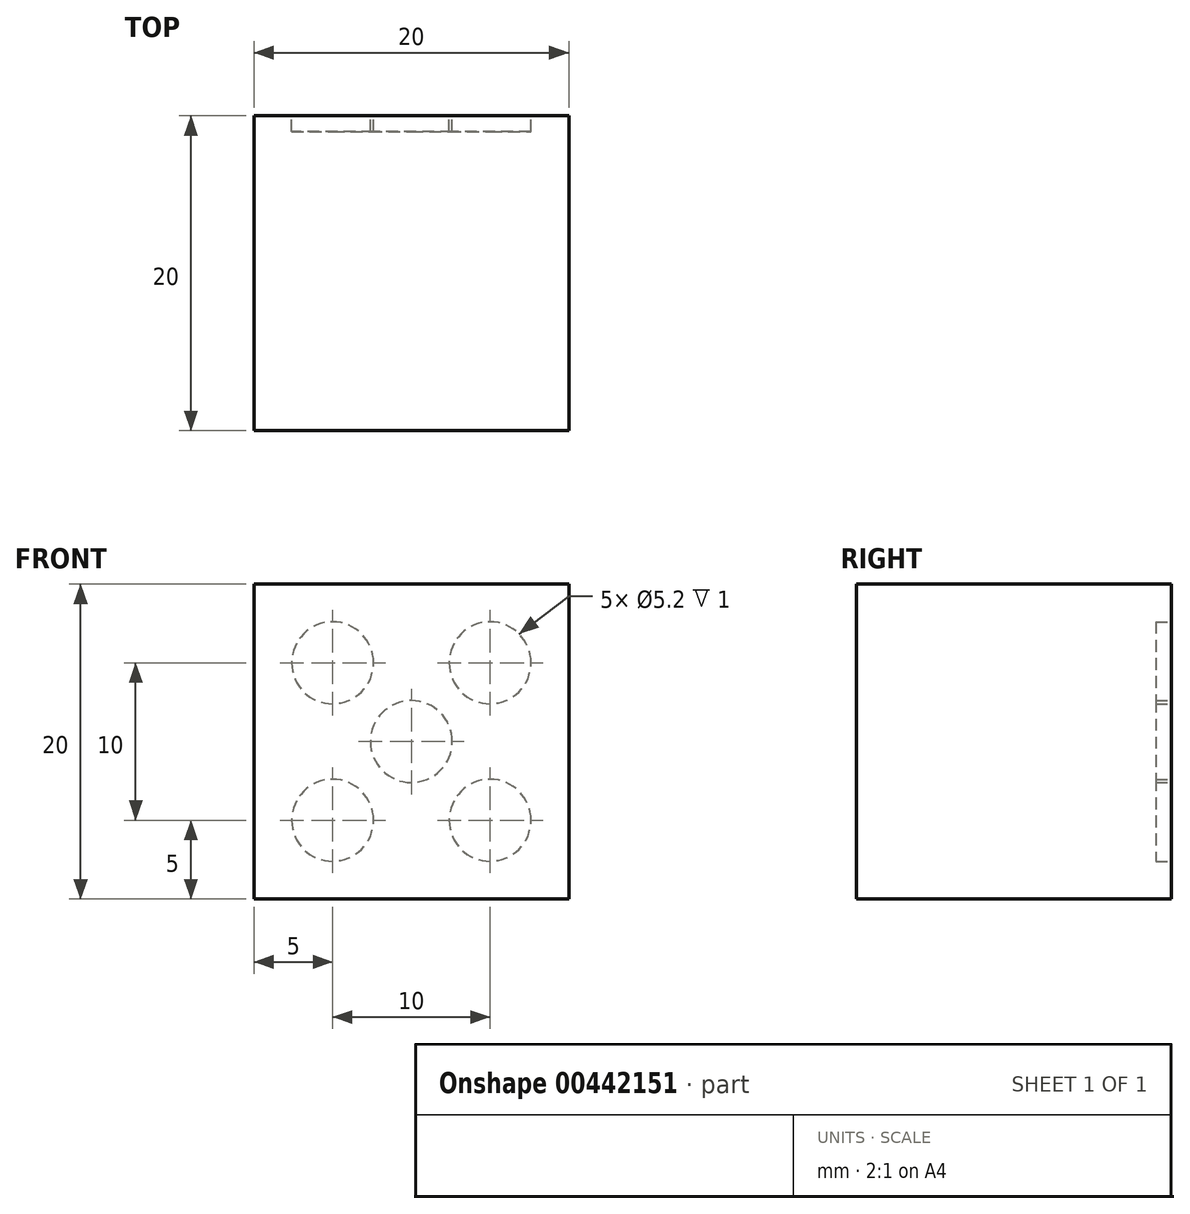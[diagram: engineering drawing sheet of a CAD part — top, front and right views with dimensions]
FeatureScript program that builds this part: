
annotation { "Feature Type Name" : "Feature", "Feature Type Description" : "" }
export const myFeature = defineFeature(function(context is Context, id is Id, definition is map)
    precondition{}
    {
        {
            var Q0;
            Q0=qCreatedBy(makeId("Front.planeOp"),FACE);
            var sketch = newSketch(context, id + "F0", { "sketchPlane" : qUnion([Q0])});
            skLineSegment(sketch, "E0.bottom", {"start": v(0, 0) * mm, "end": v(20, 0) * mm});
            skLineSegment(sketch, "E0.top", {"start": v(0, 20) * mm, "end": v(20, 20) * mm});
            skLineSegment(sketch, "E0.left", {"start": v(0, 0) * mm, "end": v(0, 20) * mm});
            skLineSegment(sketch, "E0.right", {"start": v(20, 0) * mm, "end": v(20, 20) * mm});
            skSolve(sketch);
        }
        {
            var Q0;
            Q0 = qSketchRegion(id + "F0", true);
            extrude(context, id + "F1", {"entities" : qUnion([Q0]), "depth" : 20 * mm});
        }
        {
            var Q0;
            Q0=makeQuery(id+"F1.opExtrude","CAP_FACE",FACE,{"disambiguationData":[OSD([sQuery(id+"F0.wireOp",EDGE,"E0.bottom"),sQuery(id+"F0.wireOp",EDGE,"E0.top"),sQuery(id+"F0.wireOp",EDGE,"E0.left"),sQuery(id+"F0.wireOp",EDGE,"E0.right")])],"isStart":true});
            var sketch = newSketch(context, id + "F2", { "sketchPlane" : qUnion([Q0])});
            skLineSegment(sketch, "E1", {"start": v(-10, 20) * mm, "end": v(-10, 0) * mm, "construction": true});
            skLineSegment(sketch, "E2", {"start": v(-20, 10) * mm, "end": v(0, 10) * mm, "construction": true});
            skCircle(sketch, "E3", {"center": v(-10, 10) * mm, "radius": 2.6 * mm});
            skCircle(sketch, "E4", {"center": v(-15, 15) * mm, "radius": 2.6 * mm});
            skCircle(sketch, "E5.MirrorC", {"center": v(-5, 15) * mm, "radius": 2.6 * mm});
            skCircle(sketch, "E6.MirrorC", {"center": v(-15, 5) * mm, "radius": 2.6 * mm});
            skCircle(sketch, "E7.MirrorC", {"center": v(-5, 5) * mm, "radius": 2.6 * mm});
            skSolve(sketch);
        }
        {
            var Q0;
            Q0 = qSketchRegion(id + "F2", true);
            extrude(context, id + "F3", {"entities" : qUnion([Q0]), "operationType" : NewBodyOperationType.REMOVE, "oppositeDirection" : true, "depth" : 1 * mm});
        }
    });
